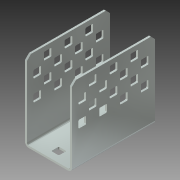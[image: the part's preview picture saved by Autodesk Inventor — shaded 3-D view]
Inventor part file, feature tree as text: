
AUTODESK INVENTOR PART (.ipt)
format: ipt  version: 2013 (Build 170138000, 138)  size: 626,176 bytes
history: native  units: in
note: dims shown in document units (in); Inventor stores cm internally (conversion verified against a paired STEP export)
features: other x37, extrude x32, sketch x7, sheet_metal_op x4, pattern_linear x3, plane x2, mirror x2
ambient origin geometry x8: Origin, YZ Plane, XZ Plane, XY Plane, X Axis, Y Axis, Z Axis, Center Point
bodies: Solid1 (feature_tree)
feature tree (87):
  sheet_metal_op  "Face1"
  sheet_metal_op  "Flange1"
  other  "Corner Chamfer1"
  plane  "Work Plane1"
  mirror  "Mirror1"
  pattern_linear  "Rectangular Pattern1"  Spacing1=1.885in  [1 undecoded]
  pattern_linear  "Rectangular Pattern2"  Spacing1=0.188in  [1 undecoded]
  plane  "Work Plane2"
  mirror  "Mirror2"
  pattern_linear  "Rectangular Pattern3"  Spacing1=0.047in  [1 undecoded]
  sketch  "Sketch1"  dims[d0=2.0in]
  other  "Plate1"
  sketch  "Sketch2"  dims[d1=1.129in]
  other  "Plate2"
  sheet_metal_op  "Bend1"
  sheet_metal_op  "Corner1"
  sketch  "Sketch3"  dims[d2=0.047in]
  sketch  "Sketch4"  dims[d3=0.047in]
  sketch  "Sketch5"  dims[d4=0.0235in]
  other  "Srf1"
  other  "Srf2"
  other  "Srf3"
  other  "Srf4"
  other  "Srf5"
  other  "Srf6"
  sketch  "Sketch6"  dims[d5=0.094in]
  other  "Srf7"
  other  "Srf8"
  other  "Srf9"
  other  "Srf10"
  other  "Srf11"
  other  "Srf12"
  other  "Srf13"
  other  "Srf14"
  other  "Srf18"
  other  "Srf19"
  other  "Srf20"
  other  "Srf15"
  other  "Srf16"
  other  "Srf17"
  other  "Srf21"
  other  "Srf22"
  other  "Srf23"
  other  "Srf24"
  other  "Srf25"
  other  "Srf26"
  other  "Srf27"
  other  "Srf28"
  sketch  "Sketch7"  dims[d6=0.047in d7=1.885in d8=90.0deg d9=0.047in d10=0.188in d11=0.047in d12=0.047in d13=0.1in d14=0.25in d15=45.0deg d16=0.182in d17=0.182in d18=0.02in d19=0.5in d20=0.206in d21=1.1811in d23=0.5in d24=0.3937in d26=1.0in d28=0.7874in d30=0.5in d31=0.3937in d33=1.0in d35=0.02in d36=0.25in d37=0.182in d38=0.182in d39=0.25in d40=1.5748in d42=0.5in d43=0.7874in d45=0.5in d48=0.047in d49=0.0in d50=0.182in d51=0.182in d52=0.02in d53=0.25in d54=1.5748in d56=0.5in d57=0.3937in d59=1.0in d61=0.047in d62=0.0in d63=1.0in d64=0.0in d65=1.1811in d67=0.5in d68=0.7874in d70=0.5in d71=1.0in d72=0.0in d73=1.5748in d75=0.5in d76=0.7874in d78=0.5in d79=1.0in d80=0.0in d81=1.5748in d83=0.5in d84=0.0in d85=0.0in d86=0.0in d87=0.0in d88=0.0in d89=0.0in d90=0.0in d91=0.0in d92=0.0in d93=0.0in d94=0.0in d95=0.0in d96=0.0in d97=0.0in d98=0.0in d99=0.0in d100=0.0in d101=0.0in d102=0.0in d103=0.0in d104=0.0in d105=0.0in d106=0.0in d107=0.0in d108=0.0in d109=0.0in d110=0.0in d111=0.0in d112=0.0in d113=0.0in d114=0.0in d115=0.0in d116=0.0in d117=0.0in d118=0.0in d119=0.0in d120=0.0in d121=0.0in d122=0.0in d123=0.0in d124=0.0in d125=0.0in d126=0.0in d127=0.0in d128=0.0in d129=0.0in d130=0.0in d131=0.0in d132=0.0in d133=0.0in d134=0.0in d135=0.0in d136=0.0in d137=0.0in d138=0.0in d139=0.0in d140=0.0in d141=0.0in d142=0.0in d143=0.0in d144=0.0in d145=0.0in d146=0.0in d147=0.0in]
  other  "Srf29"
  other  "Srf30"
  other  "Srf31"
  other  "Srf32"
  other  "Cut1"
  other  "Cut2"
  extrude  "ExtrusionSrf1"  Depth=0.047in
  extrude  "ExtrusionSrf7"  Depth=0.1in TaperAngle=45.0deg
  extrude  "ExtrusionSrf29"  Depth=0.182in
  extrude  "ExtrusionSrf2"  Depth=0.182in
  extrude  "ExtrusionSrf3"  Depth=0.02in
  extrude  "ExtrusionSrf4"  Depth=0.5in
  extrude  "ExtrusionSrf5"  Depth=0.206in
  extrude  "ExtrusionSrf6"  Depth=1.1811in
  extrude  "ExtrusionSrf8"  Depth=0.7874in
  extrude  "ExtrusionSrf9"  Depth=0.02in
  extrude  "ExtrusionSrf10"  Depth=0.25in
  extrude  "ExtrusionSrf11"  Depth=0.182in
  extrude  "ExtrusionSrf12"  Depth=0.182in
  extrude  "ExtrusionSrf13"  Depth=0.25in
  extrude  "ExtrusionSrf14"  Depth=1.5748in
  extrude  "ExtrusionSrf15"  Depth=0.047in
  extrude  "ExtrusionSrf16"  TaperAngle=0.0deg  [1 undecoded]
  extrude  "ExtrusionSrf17"  Depth=0.182in
  extrude  "ExtrusionSrf18"  Depth=0.182in
  extrude  "ExtrusionSrf19"  Depth=0.02in
  extrude  "ExtrusionSrf20"  Depth=0.25in
  extrude  "ExtrusionSrf21"  Depth=1.5748in
  extrude  "ExtrusionSrf22"  Depth=0.047in
  extrude  "ExtrusionSrf23"  TaperAngle=0.0deg  [1 undecoded]
  extrude  "ExtrusionSrf24"  Depth=1.0in TaperAngle=0.0deg
  extrude  "ExtrusionSrf25"  Depth=1.1811in
  extrude  "ExtrusionSrf26"  Depth=0.7874in
  extrude  "ExtrusionSrf27"  Depth=1.0in TaperAngle=0.0deg
  extrude  "ExtrusionSrf28"  Depth=1.5748in
  extrude  "ExtrusionSrf30"  Depth=0.7874in
  extrude  "ExtrusionSrf31"  Depth=1.0in TaperAngle=0.0deg
  extrude  "ExtrusionSrf32"  Depth=1.5748in
note: 5 required parameter values undecoded (feature->parameter linkage not recoverable at this tier; creation-order binding heuristic only, values carry confidence <= 0.55)
